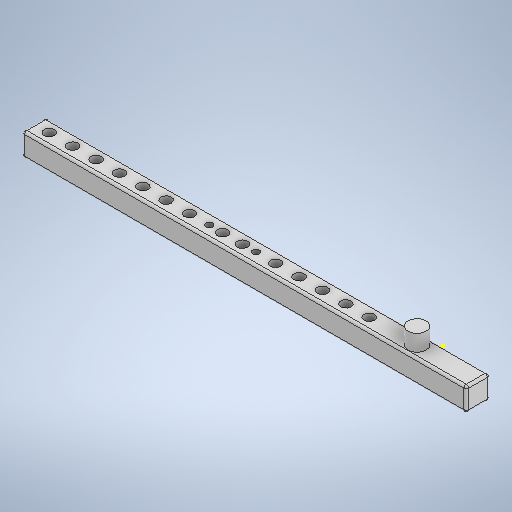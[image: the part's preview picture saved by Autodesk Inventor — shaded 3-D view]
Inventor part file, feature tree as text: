
AUTODESK INVENTOR PART (.ipt)
format: ipt  version: 2025.2 (Build 292293000, 293)  size: 356,864 bytes
history: native  units: in
note: dims shown in document units (in); Inventor stores cm internally (conversion verified against a paired STEP export)
features: sketch x9, extrude x8, thread x2, fillet x2
ambient origin geometry x8: Origin, YZ Plane, XZ Plane, XY Plane, X Axis, Y Axis, Z Axis, Center Point
bodies: Solid1 (feature_tree)
feature tree (21):
  extrude  "Extrusion1"  Depth=0.3937in
  sketch  "Sketch2"  dims[d8=0.1181in d9=0.1181in]
  extrude  "Extrusion2"  Depth=0.3937in
  extrude  "Extrusion3"  Depth=0.1181in
  extrude  "Extrusion4"  Depth=0.3937in TaperAngle=0.0deg
  extrude  "Extrusion5"  Depth=0.3937in
  thread  "Thread1"  [1 undecoded]
  thread  "Thread2"  [1 undecoded]
  extrude  "Extrusion6"  Depth=0.3937in TaperAngle=0.0deg
  extrude  "Extrusion7"  Depth=0.3937in TaperAngle=0.0deg
  extrude  "Extrusion8"  Depth=0.0394in
  sketch  "Sketch7"
  fillet  "Fillet3"  Radius=0.0394in
  fillet  "Fillet4"  [1 undecoded]
  sketch  "Sketch1"  dims[d0=6.6929in d1=0.3937in]
  sketch  "Sketch3"  dims[d14=0.2756in d15=0.0in d18=2.7559in d20=0.3937in d21=0.3937in d23=0.3937in d30=2.3622in d32=0.3937in d33=0.3937in d35=0.3937in d37=0.3937in d38=0.0in]
  sketch  "Sketch Rectangular Pattern1"  dims[d2=0.3937in d3=0.0in d4=0.0866in]
  sketch  "Sketch Rectangular Pattern2"  dims[d10=0.3937in d11=0.0in d12=0.3937in d13=0.0in]
  sketch  "Sketch4"  dims[d39=0.3937in d40=0.0in d41=0.3937in d42=0.0in]
  sketch  "Sketch5"  dims[d44=0.3937in d45=0.0in d46=0.3937in d47=0.0in]
  sketch  "Sketch6"  dims[d49=0.3937in d50=0.0in d51=0.0394in d52=0.0394in]
note: 3 required parameter values undecoded (feature->parameter linkage not recoverable at this tier; creation-order binding heuristic only, values carry confidence <= 0.55)
